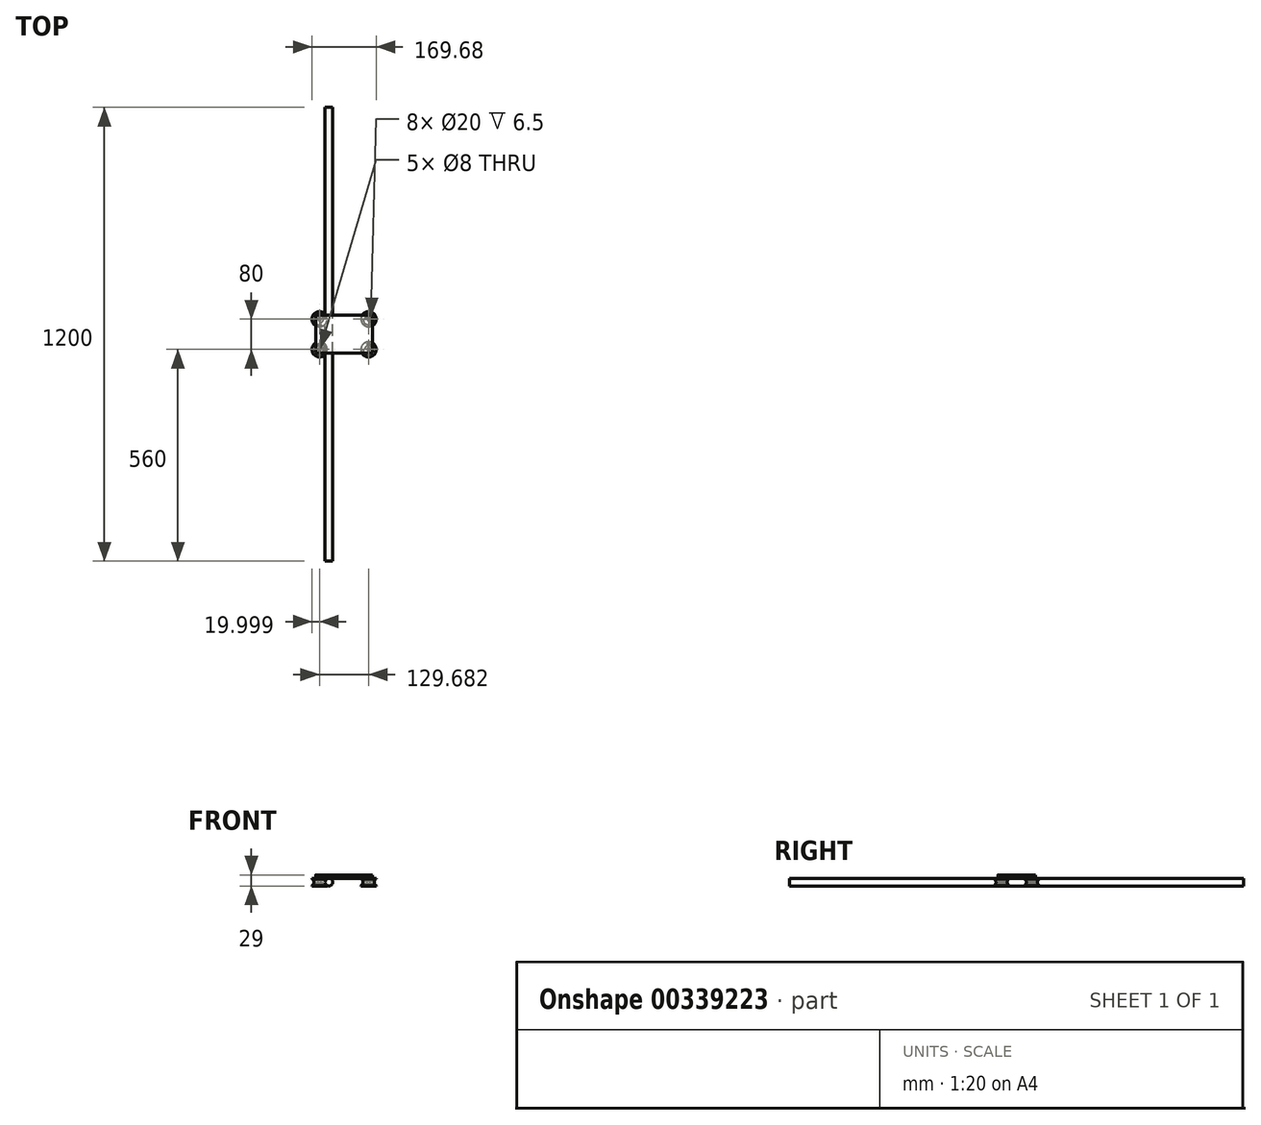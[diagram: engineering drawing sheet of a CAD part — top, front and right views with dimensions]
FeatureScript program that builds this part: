
annotation { "Feature Type Name" : "Feature", "Feature Type Description" : "" }
export const myFeature = defineFeature(function(context is Context, id is Id, definition is map)
    precondition{}
    {
        {
            var Q0;
            Q0=qCreatedBy(makeId("Front.planeOp"),FACE);
            var sketch = newSketch(context, id + "F0", { "sketchPlane" : qUnion([Q0])});
            skCircle(sketch, "E0", {"center": v(-40, 0) * mm, "radius": 10 * mm});
            skCircle(sketch, "E1.MirrorC", {"center": v(40, 0) * mm, "radius": 10 * mm});
            skSolve(sketch);
        }
        {
            var Q0;
            Q0=makeQuery(id+"F0.imprint","IMPRINT",FACE,{"disambiguationData":[TD([[makeQuery(id+"F0.imprint","IMPRINT",EDGE,{"derivedFrom":sQuery(id+"F0.wireOp",EDGE,"E0")}),1.0]])]});
            var Q1;
            Q1=makeQuery(id+"F0.imprint","IMPRINT",FACE,{"disambiguationData":[TD([[makeQuery(id+"F0.imprint","IMPRINT",EDGE,{"derivedFrom":sQuery(id+"F0.wireOp",EDGE,"E1.MirrorC")}),-1.0]])]});
            extrude(context, id + "F1", {"entities" : qUnion([Q0, Q1]), "endBound" : BoundingType.SYMMETRIC, "depth" : 1200 * mm});
        }
        {
            var Q0;
            Q0=qCreatedBy(makeId("Front.planeOp"),FACE);
            var sketch = newSketch(context, id + "F2", { "sketchPlane" : qUnion([Q0])});
            skArc(sketch, "E2.0", {"start": v(-44.84, 8.75) * mm, "mid": v(-50, 0) * mm, "end": v(-44.84, -8.75) * mm});
            skLineSegment(sketch, "E3", {"start": v(-44.84, 8.75) * mm, "end": v(-44.84, 10) * mm});
            skLineSegment(sketch, "E4", {"start": v(-44.84, -8.75) * mm, "end": v(-44.84, -10) * mm});
            skLineSegment(sketch, "E5", {"start": v(-44.84, 10) * mm, "end": v(-54.84, 10) * mm});
            skLineSegment(sketch, "E6", {"start": v(-54.84, 10) * mm, "end": v(-54.84, 3.5) * mm});
            skLineSegment(sketch, "E7", {"start": v(-54.84, -10) * mm, "end": v(-44.84, -10) * mm});
            skPoint(sketch, "E8.start.orphan", {"position": v(-54.84, 0) * mm});
            skLineSegment(sketch, "E9", {"start": v(-54.84, 3.5) * mm, "end": v(-60.84, 3.5) * mm});
            skLineSegment(sketch, "E10", {"start": v(-64.84, 3.5) * mm, "end": v(-64.84, -3.5) * mm, "construction": true});
            skLineSegment(sketch, "E11", {"start": v(-60.84, -3.5) * mm, "end": v(-54.84, -3.5) * mm});
            skLineSegment(sketch, "E12.trimOffspring", {"start": v(-54.84, -3.5) * mm, "end": v(-54.84, -10) * mm});
            skLineSegment(sketch, "E13", {"start": v(-60.84, -3.5) * mm, "end": v(-60.84, 3.5) * mm});
            skLineSegment(sketch, "E14", {"start": v(-40, 8.7) * mm, "end": v(-40, -6.73) * mm, "construction": true});
            skLineSegment(sketch, "E15.MirrorCS", {"start": v(-35.16, 10) * mm, "end": v(-25.16, 10) * mm});
            skLineSegment(sketch, "E16.MirrorCS", {"start": v(-25.16, 10) * mm, "end": v(-25.16, 3.5) * mm});
            skLineSegment(sketch, "E17.MirrorCS", {"start": v(-35.16, 8.75) * mm, "end": v(-35.16, 10) * mm});
            skArc(sketch, "E18.MirrorCS", {"start": v(-35.16, 8.75) * mm, "mid": v(-30, 0) * mm, "end": v(-35.16, -8.75) * mm});
            skLineSegment(sketch, "E19.MirrorCS", {"start": v(-35.16, -8.75) * mm, "end": v(-35.16, -10) * mm});
            skLineSegment(sketch, "E20.MirrorCS", {"start": v(-25.16, -10) * mm, "end": v(-35.16, -10) * mm});
            skLineSegment(sketch, "E21.MirrorCS", {"start": v(-25.16, -3.5) * mm, "end": v(-25.16, -10) * mm});
            skLineSegment(sketch, "E22.MirrorCS", {"start": v(-19.16, -3.5) * mm, "end": v(-25.16, -3.5) * mm});
            skLineSegment(sketch, "E23.MirrorCS", {"start": v(-19.16, -3.5) * mm, "end": v(-19.16, 3.5) * mm});
            skLineSegment(sketch, "E24.MirrorCS", {"start": v(-25.16, 3.5) * mm, "end": v(-19.16, 3.5) * mm});
            skLineSegment(sketch, "E25.MirrorCS", {"start": v(-15.16, 3.5) * mm, "end": v(-15.16, -3.5) * mm, "construction": true});
            skSolve(sketch);
        }
        {
            var Q0;
            Q0=makeQuery(id+"F2.imprint","IMPRINT",FACE,{"disambiguationData":[TD([[makeQuery(id+"F2.imprint","IMPRINT",EDGE,{"derivedFrom":sQuery(id+"F2.wireOp",EDGE,"E2.0")}),-1.0]])]});
            var Q1;
            Q1=sQuery(id+"F2.wireOp",EDGE,"E10");
            revolve(context, id + "F3", {"operationType" : NewBodyOperationType.ADD, "entities" : qUnion([Q0]), "axis" : qUnion([Q1]), "revolveType" : RevolveType.FULL});
        }
        {
            var Q0;
            Q0=makeQuery(id+"F3.opRevolve","SWEPT_BODY",BODY,{"disambiguationData":[OSD([sQuery(id+"F2.wireOp",EDGE,"E2.0"),sQuery(id+"F2.wireOp",EDGE,"E3"),sQuery(id+"F2.wireOp",EDGE,"E4"),sQuery(id+"F2.wireOp",EDGE,"E5"),sQuery(id+"F2.wireOp",EDGE,"E6"),sQuery(id+"F2.wireOp",EDGE,"E7"),sQuery(id+"F2.wireOp",EDGE,"E9"),sQuery(id+"F2.wireOp",EDGE,"E11"),sQuery(id+"F2.wireOp",EDGE,"E12.trimOffspring"),sQuery(id+"F2.wireOp",EDGE,"E13")])]});
            var Q1;
            Q1=qCreatedBy(makeId("Right.planeOp"),FACE);
            mirror(context, id + "F4", {"operationType" : NewBodyOperationType.ADD, "entities" : qUnion([Q0]), "mirrorPlane" : qUnion([Q1])});
        }
        {
            var Q0;
            Q0=makeQuery(id+"F3.opRevolve","SWEPT_FACE",FACE,{"disambiguationData":[OSD([sQuery(id+"F2.wireOp",EDGE,"E5")])]});
            cPlane(context, id + "F5", {"entities" : qUnion([Q0]), "cplaneType" : CPlaneType.OFFSET, "offset" : 0 * mm, "width" : 150 * mm, "height" : 150 * mm});
        }
        {
            var Q0;
            Q0=makeQuery(id+"F3.opRevolve","SWEPT_BODY",BODY,{"disambiguationData":[OSD([sQuery(id+"F2.wireOp",EDGE,"E2.0"),sQuery(id+"F2.wireOp",EDGE,"E3"),sQuery(id+"F2.wireOp",EDGE,"E4"),sQuery(id+"F2.wireOp",EDGE,"E5"),sQuery(id+"F2.wireOp",EDGE,"E6"),sQuery(id+"F2.wireOp",EDGE,"E7"),sQuery(id+"F2.wireOp",EDGE,"E9"),sQuery(id+"F2.wireOp",EDGE,"E11"),sQuery(id+"F2.wireOp",EDGE,"E12.trimOffspring"),sQuery(id+"F2.wireOp",EDGE,"E13")])]});
            var Q1;
            Q1=makeQuery(id+"F4.opPattern","COPY",BODY,{"derivedFrom":makeQuery(id+"F3.opRevolve","SWEPT_BODY",BODY,{"disambiguationData":[OSD([sQuery(id+"F2.wireOp",EDGE,"E2.0"),sQuery(id+"F2.wireOp",EDGE,"E3"),sQuery(id+"F2.wireOp",EDGE,"E4"),sQuery(id+"F2.wireOp",EDGE,"E5"),sQuery(id+"F2.wireOp",EDGE,"E6"),sQuery(id+"F2.wireOp",EDGE,"E7"),sQuery(id+"F2.wireOp",EDGE,"E9"),sQuery(id+"F2.wireOp",EDGE,"E11"),sQuery(id+"F2.wireOp",EDGE,"E12.trimOffspring"),sQuery(id+"F2.wireOp",EDGE,"E13")])]}),"instanceName":"1"});
            transform(context, id + "F6", {"entities" : qUnion([Q0, Q1]), "transformType" : TransformType.TRANSLATION_3D, "dx" : 0 * mm, "dy" : 40 * mm, "dz" : 0 * mm, "makeCopy" : false});
        }
        {
            var Q0;
            Q0=makeQuery(id+"F3.opRevolve","SWEPT_BODY",BODY,{"disambiguationData":[OSD([sQuery(id+"F2.wireOp",EDGE,"E2.0"),sQuery(id+"F2.wireOp",EDGE,"E3"),sQuery(id+"F2.wireOp",EDGE,"E4"),sQuery(id+"F2.wireOp",EDGE,"E5"),sQuery(id+"F2.wireOp",EDGE,"E6"),sQuery(id+"F2.wireOp",EDGE,"E7"),sQuery(id+"F2.wireOp",EDGE,"E9"),sQuery(id+"F2.wireOp",EDGE,"E11"),sQuery(id+"F2.wireOp",EDGE,"E12.trimOffspring"),sQuery(id+"F2.wireOp",EDGE,"E13")])]});
            var Q1;
            Q1=makeQuery(id+"F4.opPattern","COPY",BODY,{"derivedFrom":makeQuery(id+"F3.opRevolve","SWEPT_BODY",BODY,{"disambiguationData":[OSD([sQuery(id+"F2.wireOp",EDGE,"E2.0"),sQuery(id+"F2.wireOp",EDGE,"E3"),sQuery(id+"F2.wireOp",EDGE,"E4"),sQuery(id+"F2.wireOp",EDGE,"E5"),sQuery(id+"F2.wireOp",EDGE,"E6"),sQuery(id+"F2.wireOp",EDGE,"E7"),sQuery(id+"F2.wireOp",EDGE,"E9"),sQuery(id+"F2.wireOp",EDGE,"E11"),sQuery(id+"F2.wireOp",EDGE,"E12.trimOffspring"),sQuery(id+"F2.wireOp",EDGE,"E13")])]}),"instanceName":"1"});
            var Q2;
            Q2=qCreatedBy(makeId("Front.planeOp"),FACE);
            mirror(context, id + "F7", {"entities" : qUnion([Q0, Q1]), "mirrorPlane" : qUnion([Q2])});
        }
        {
            var Q0;
            Q0=makeQuery(id+"F4.opPattern","COPY",FACE,{"derivedFrom":makeQuery(id+"F3.opRevolve","SWEPT_FACE",FACE,{"disambiguationData":[OSD([sQuery(id+"F2.wireOp",EDGE,"E9")])]}),"instanceName":"1"});
            cPlane(context, id + "F8", {"entities" : qUnion([Q0]), "cplaneType" : CPlaneType.OFFSET, "offset" : 0 * mm, "width" : 150 * mm, "height" : 150 * mm});
        }
        {
            var Q0;
            Q0=qCreatedBy(id+"F8.planeOp",FACE);
            var sketch = newSketch(context, id + "F9", { "sketchPlane" : qUnion([Q0])});
            skCircle(sketch, "E26.0", {"center": v(64.84, 40) * mm, "radius": 4 * mm});
            skCircle(sketch, "E27", {"center": v(64.84, 40) * mm, "radius": 9 * mm});
            skSolve(sketch);
        }
        {
            var Q0;
            Q0=makeQuery(id+"F9.imprint","IMPRINT",FACE,{"disambiguationData":[TD([[makeQuery(id+"F9.imprint","IMPRINT",EDGE,{"derivedFrom":sQuery(id+"F9.wireOp",EDGE,"E26.0")}),-1.0]])]});
            extrude(context, id + "F10", {"entities" : qUnion([Q0]), "depth" : 7 * mm});
        }
        {
            var Q0;
            Q0=qCreatedBy(id+"F5.planeOp",FACE);
            var sketch = newSketch(context, id + "F11", { "sketchPlane" : qUnion([Q0])});
            skLineSegment(sketch, "E28", {"start": v(0, 0) * mm, "end": v(-75, 0) * mm, "construction": true});
            skLineSegment(sketch, "E29.MirrorCS", {"start": v(0, 0) * mm, "end": v(75, 0) * mm, "construction": true});
            skLineSegment(sketch, "E30.bottom", {"start": v(-70, -50) * mm, "end": v(70, -50) * mm});
            skLineSegment(sketch, "E30.top", {"start": v(-70, 50) * mm, "end": v(70, 50) * mm});
            skLineSegment(sketch, "E30.left", {"start": v(-75, -45) * mm, "end": v(-75, 45) * mm});
            skLineSegment(sketch, "E30.right", {"start": v(75, -45) * mm, "end": v(75, 45) * mm});
            skPoint(sketch, "E30.middle", {"position": v(0, 0) * mm});
            skPoint(sketch, "E31.visualSharp", {"position": v(-75, 50) * mm});
            skArc(sketch, "E31.filletArc", {"start": v(-70, 50) * mm, "mid": v(-73.54, 48.54) * mm, "end": v(-75, 45) * mm});
            skPoint(sketch, "E32.visualSharp", {"position": v(75, 50) * mm});
            skArc(sketch, "E32.filletArc", {"start": v(75, 45) * mm, "mid": v(73.54, 48.54) * mm, "end": v(70, 50) * mm});
            skPoint(sketch, "E33.visualSharp", {"position": v(75, -50) * mm});
            skArc(sketch, "E33.filletArc", {"start": v(70, -50) * mm, "mid": v(73.54, -48.54) * mm, "end": v(75, -45) * mm});
            skPoint(sketch, "E34.visualSharp", {"position": v(-75, -50) * mm});
            skArc(sketch, "E34.filletArc", {"start": v(-75, -45) * mm, "mid": v(-73.54, -48.54) * mm, "end": v(-70, -50) * mm});
            skSolve(sketch);
        }
        {
            var Q0;
            Q0=makeQuery(id+"F11.imprint","IMPRINT",FACE,{"disambiguationData":[TD([[makeQuery(id+"F11.imprint","IMPRINT",EDGE,{"derivedFrom":sQuery(id+"F11.wireOp",EDGE,"E30.bottom")}),1.0]])]});
            extrude(context, id + "F12", {"entities" : qUnion([Q0]), "depth" : 9 * mm});
        }
    });
